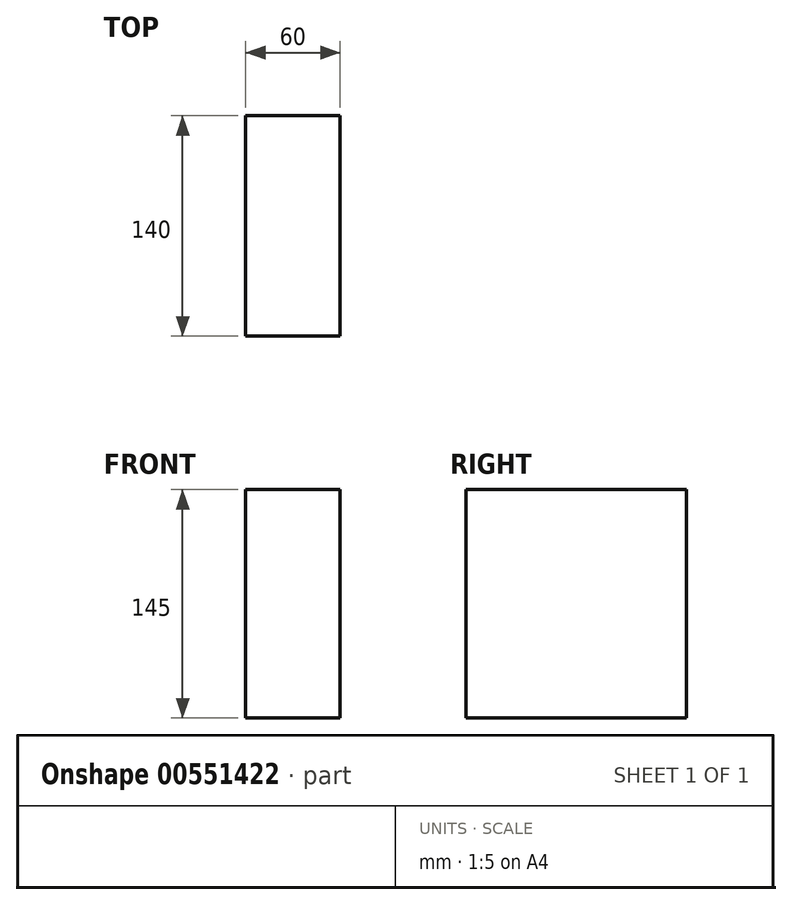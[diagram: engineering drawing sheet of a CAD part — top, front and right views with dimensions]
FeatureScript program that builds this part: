
annotation { "Feature Type Name" : "Feature", "Feature Type Description" : "" }
export const myFeature = defineFeature(function(context is Context, id is Id, definition is map)
    precondition{}
    {
        {
            var Q0;
            Q0=qCreatedBy(makeId("Front.planeOp"),FACE);
            var sketch = newSketch(context, id + "F0", { "sketchPlane" : qUnion([Q0])});
            skLineSegment(sketch, "E0.bottom", {"start": v(30, 72.5) * mm, "end": v(-30, 72.5) * mm});
            skLineSegment(sketch, "E0.top", {"start": v(30, -72.5) * mm, "end": v(-30, -72.5) * mm});
            skLineSegment(sketch, "E0.left", {"start": v(30, 72.5) * mm, "end": v(30, -72.5) * mm});
            skLineSegment(sketch, "E0.right", {"start": v(-30, 72.5) * mm, "end": v(-30, -72.5) * mm});
            skPoint(sketch, "E0.middle", {"position": v(0, 0) * mm});
            skSolve(sketch);
        }
        {
            var Q0;
            Q0=makeQuery(id+"F0.imprint","IMPRINT",FACE,{"disambiguationData":[TD([[makeQuery(id+"F0.imprint","IMPRINT",EDGE,{"derivedFrom":sQuery(id+"F0.wireOp",EDGE,"E0.bottom")}),1.0]])]});
            extrude(context, id + "F1", {"entities" : qUnion([Q0]), "depth" : 140 * mm, "offsetDistance" : 25.4 * mm});
        }
    });
